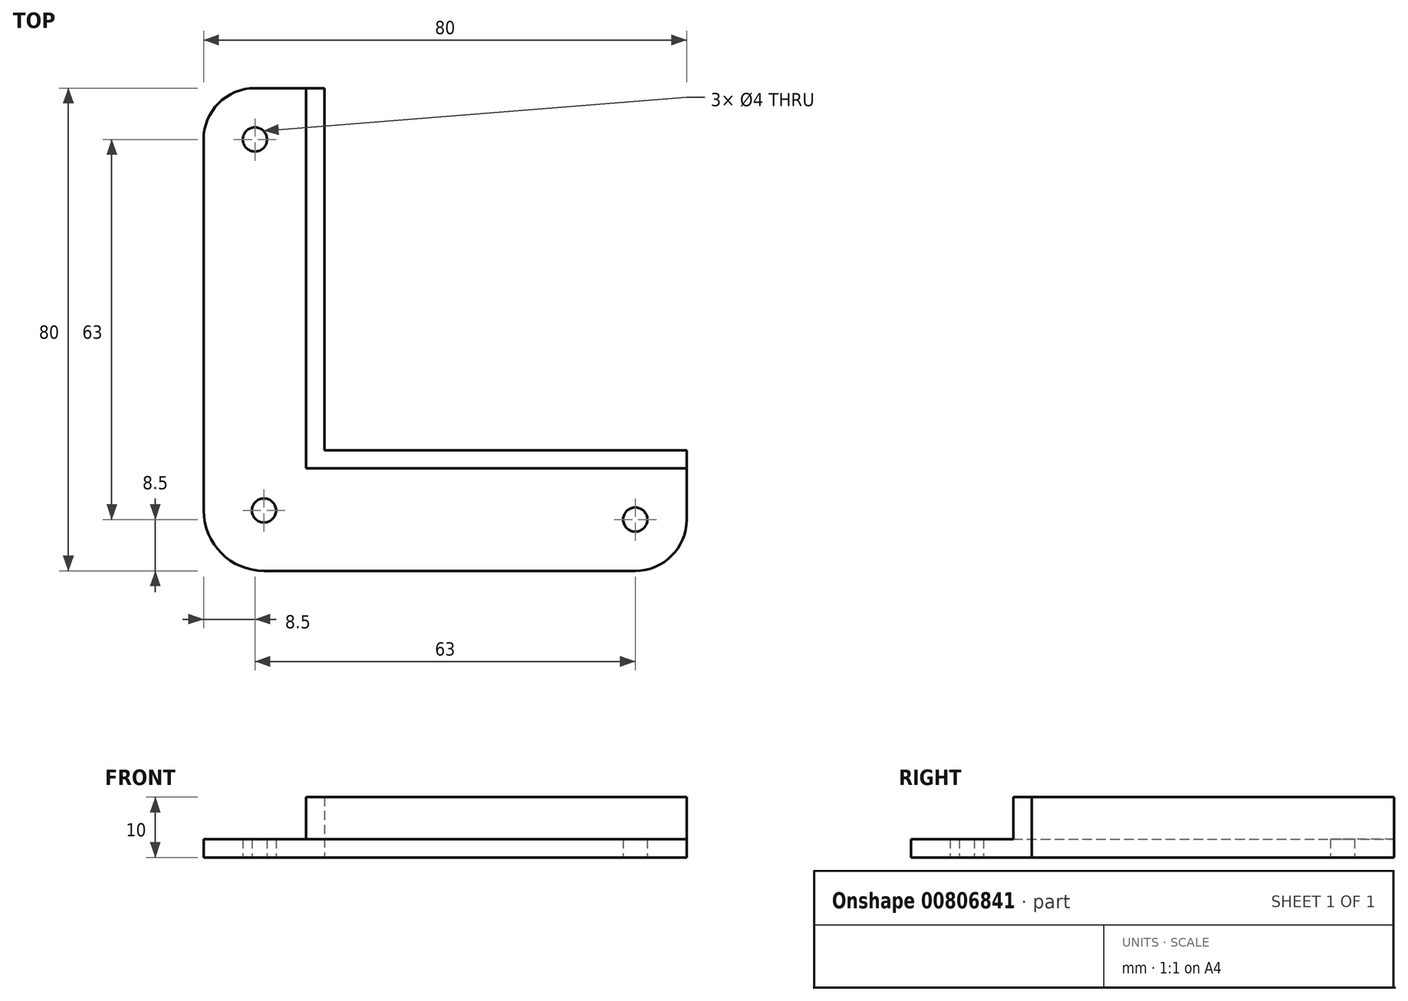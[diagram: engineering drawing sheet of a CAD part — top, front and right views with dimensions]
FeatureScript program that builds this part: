
annotation { "Feature Type Name" : "Feature", "Feature Type Description" : "" }
export const myFeature = defineFeature(function(context is Context, id is Id, definition is map)
    precondition{}
    {
        {
            var Q0;
            Q0=qCreatedBy(makeId("Top.planeOp"),FACE);
            var sketch = newSketch(context, id + "F0", { "sketchPlane" : qUnion([Q0])});
            skLineSegment(sketch, "E0.bottom", {"start": v(0, 0) * mm, "end": v(20, 0) * mm});
            skLineSegment(sketch, "E0.top", {"start": v(0, 80) * mm, "end": v(20, 80) * mm});
            skLineSegment(sketch, "E0.left", {"start": v(0, 0) * mm, "end": v(0, 80) * mm});
            skLineSegment(sketch, "E0.right", {"start": v(20, 0) * mm, "end": v(20, 80) * mm});
            skLineSegment(sketch, "E1.bottom", {"start": v(10, 0) * mm, "end": v(71.5, 0) * mm});
            skLineSegment(sketch, "E1.top", {"start": v(0, 20) * mm, "end": v(80, 20) * mm});
            skLineSegment(sketch, "E1.left", {"start": v(0, 10) * mm, "end": v(0, 20) * mm});
            skLineSegment(sketch, "E1.right", {"start": v(80, 0) * mm, "end": v(80, 20) * mm});
            skLineSegment(sketch, "E2.bottom", {"start": v(80, 20) * mm, "end": v(20, 20) * mm});
            skLineSegment(sketch, "E2.top", {"start": v(80, 17) * mm, "end": v(20, 17) * mm});
            skLineSegment(sketch, "E2.left", {"start": v(80, 20) * mm, "end": v(80, 17) * mm});
            skLineSegment(sketch, "E2.right", {"start": v(20, 20) * mm, "end": v(20, 17) * mm});
            skLineSegment(sketch, "E3.bottom", {"start": v(20, 17) * mm, "end": v(17, 17) * mm});
            skLineSegment(sketch, "E3.top", {"start": v(20, 80) * mm, "end": v(17, 80) * mm});
            skLineSegment(sketch, "E3.left", {"start": v(20, 17) * mm, "end": v(20, 80) * mm});
            skLineSegment(sketch, "E3.right", {"start": v(17, 17) * mm, "end": v(17, 80) * mm});
            skLineSegment(sketch, "E4.bottom", {"start": v(8.5, 80) * mm, "end": v(17, 80) * mm});
            skLineSegment(sketch, "E4.top", {"start": v(0, 63) * mm, "end": v(17, 63) * mm});
            skLineSegment(sketch, "E4.left", {"start": v(0, 71.5) * mm, "end": v(0, 63) * mm});
            skLineSegment(sketch, "E4.right", {"start": v(17, 80) * mm, "end": v(17, 63) * mm});
            skLineSegment(sketch, "E5.bottom", {"start": v(63, 17) * mm, "end": v(80, 17) * mm});
            skLineSegment(sketch, "E5.top", {"start": v(63, 0) * mm, "end": v(80, 0) * mm});
            skLineSegment(sketch, "E5.left", {"start": v(63, 17) * mm, "end": v(63, 0) * mm});
            skLineSegment(sketch, "E5.right", {"start": v(80, 17) * mm, "end": v(80, 8.5) * mm});
            skCircle(sketch, "E6", {"center": v(8.5, 71.5) * mm, "radius": 2 * mm});
            skPoint(sketch, "E6.centerSnap0", {"position": v(8.5, 80) * mm});
            skPoint(sketch, "E6.centerSnap1", {"position": v(0, 71.5) * mm});
            skCircle(sketch, "E7", {"center": v(71.5, 8.5) * mm, "radius": 2 * mm});
            skPoint(sketch, "E7.centerSnap0", {"position": v(63, 8.5) * mm});
            skPoint(sketch, "E7.centerSnap1", {"position": v(71.5, 0) * mm});
            skPoint(sketch, "E8.visualSharp", {"position": v(0, 80) * mm});
            skArc(sketch, "E8.filletArc", {"start": v(8.5, 80) * mm, "mid": v(2.49, 77.51) * mm, "end": v(0, 71.5) * mm});
            skPoint(sketch, "E9.visualSharp", {"position": v(80, 0) * mm});
            skArc(sketch, "E9.filletArc", {"start": v(71.5, 0) * mm, "mid": v(77.51, 2.49) * mm, "end": v(80, 8.5) * mm});
            skPoint(sketch, "E10.visualSharp", {"position": v(0, 0) * mm});
            skArc(sketch, "E10.filletArc", {"start": v(0, 10) * mm, "mid": v(2.93, 2.93) * mm, "end": v(10, 0) * mm});
            skCircle(sketch, "E11", {"center": v(10, 10) * mm, "radius": 2 * mm});
            skSolve(sketch);
        }
        {
            var Q0;
            {var subQ0=sQuery(id+"F0.wireOp",EDGE,"E4.top");Q0=makeQuery(id+"F0.imprint","IMPRINT",FACE,{"disambiguationData":[TD([[makeQuery(id+"F0.imprint","IMPRINT",EDGE,{"derivedFrom":subQ0}),1.0]])]});}
            var Q1;
            {var subQ3=sQuery(id+"F0.wireOp",EDGE,"E4.top");Q1=makeQuery(id+"F0.imprint","IMPRINT",FACE,{"disambiguationData":[TD([[makeQuery(id+"F0.imprint","IMPRINT",EDGE,{"derivedFrom":subQ3}),-1.0]])]});}
            var Q2;
            {var subQ9=sQuery(id+"F0.wireOp",EDGE,"E3.bottom");Q2=makeQuery(id+"F0.imprint","IMPRINT",FACE,{"disambiguationData":[TD([[makeQuery(id+"F0.imprint","IMPRINT",EDGE,{"derivedFrom":subQ9}),1.0]])]});}
            var Q3;
            {var subQ5=sQuery(id+"F0.wireOp",EDGE,"E5.left");Q3=makeQuery(id+"F0.imprint","IMPRINT",FACE,{"disambiguationData":[TD([[makeQuery(id+"F0.imprint","IMPRINT",EDGE,{"derivedFrom":subQ5}),-1.0]])]});}
            var Q4;
            {var subQ0=sQuery(id+"F0.wireOp",EDGE,"E5.left");Q4=makeQuery(id+"F0.imprint","IMPRINT",FACE,{"disambiguationData":[TD([[makeQuery(id+"F0.imprint","IMPRINT",EDGE,{"derivedFrom":subQ0}),1.0]])]});}
            extrude(context, id + "F1", {"entities" : qUnion([Q0, Q1, Q2, Q3, Q4]), "depth" : 3 * mm, "offsetDistance" : 25 * mm});
        }
        {
            var Q0;
            {var subQ1=sQuery(id+"F0.wireOp",EDGE,"E0.right");var subQ5=sQuery(id+"F0.wireOp",EDGE,"E0.top");var subQ6=makeQuery(id+"F0.imprint","INTERSECT",VERTEX,{"derivedFrom":[subQ5,subQ1]});Q0=makeQuery(id+"F0.imprint","IMPRINT",FACE,{"disambiguationData":[TD([[makeQuery(id+"F0.imprint","IMPRINT",EDGE,{"disambiguationData":[TD([[subQ6,1.0]])],"derivedFrom":subQ5}),-1.0]])]});}
            var Q1;
            {var subQ2=sQuery(id+"F0.wireOp",EDGE,"E0.right");var subQ5=sQuery(id+"F0.wireOp",EDGE,"E1.top");var subQ8=makeQuery(id+"F0.imprint","INTERSECT",VERTEX,{"derivedFrom":[subQ2,subQ5]});Q1=makeQuery(id+"F0.imprint","IMPRINT",FACE,{"disambiguationData":[TD([[makeQuery(id+"F0.imprint","IMPRINT",EDGE,{"disambiguationData":[TD([[subQ8,-1.0]])],"derivedFrom":subQ5}),-1.0]])]});}
            var Q2;
            {var subQ3=sQuery(id+"F0.wireOp",EDGE,"E3.bottom");Q2=makeQuery(id+"F0.imprint","IMPRINT",FACE,{"disambiguationData":[TD([[makeQuery(id+"F0.imprint","IMPRINT",EDGE,{"derivedFrom":subQ3}),-1.0]])]});}
            extrude(context, id + "F2", {"entities" : qUnion([Q0, Q1, Q2]), "operationType" : NewBodyOperationType.ADD, "depth" : 10 * mm, "offsetDistance" : 25 * mm});
        }
    });
